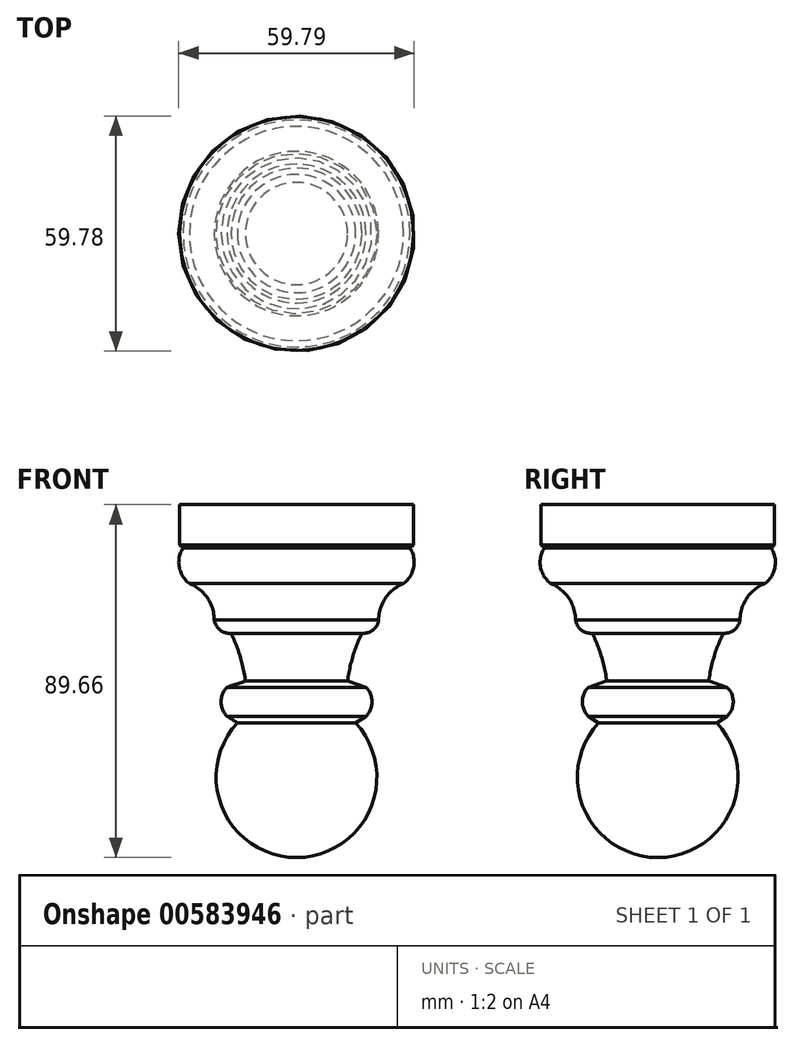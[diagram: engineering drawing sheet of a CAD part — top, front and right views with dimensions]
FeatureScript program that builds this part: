
annotation { "Feature Type Name" : "Feature", "Feature Type Description" : "" }
export const myFeature = defineFeature(function(context is Context, id is Id, definition is map)
    precondition{}
    {
        {
            var Q0;
            Q0=qCreatedBy(makeId("Front.planeOp"),FACE);
            var sketch = newSketch(context, id + "F0", { "sketchPlane" : qUnion([Q0])});
            skLineSegment(sketch, "E0.left", {"start": v(34.75, 61.97) * mm, "end": v(34.75, 51.69) * mm});
            skArc(sketch, "E1", {"start": v(32.3, 41.95) * mm, "mid": v(34.87, 46.17) * mm, "end": v(33.91, 51.02) * mm});
            skLineSegment(sketch, "E2", {"start": v(34.75, 51.69) * mm, "end": v(33.91, 51.02) * mm});
            skArc(sketch, "E3", {"start": v(32.3, 41.95) * mm, "mid": v(27.72, 38.27) * mm, "end": v(25.97, 32.66) * mm});
            skArc(sketch, "E4", {"start": v(21.7, 29.32) * mm, "mid": v(24.5, 30.13) * mm, "end": v(25.97, 32.66) * mm});
            skArc(sketch, "E5", {"start": v(21.7, 29.32) * mm, "mid": v(19.38, 23.38) * mm, "end": v(18.07, 17.13) * mm});
            skLineSegment(sketch, "E6", {"start": v(18.07, 17.13) * mm, "end": v(22.73, 15.6) * mm});
            skArc(sketch, "E7", {"start": v(22.73, 8.23) * mm, "mid": v(24.25, 11.92) * mm, "end": v(22.73, 15.6) * mm});
            skLineSegment(sketch, "E8", {"start": v(22.73, 8.23) * mm, "end": v(20.12, 6.57) * mm});
            skLineSegment(sketch, "E9", {"start": v(5.09, -7.39) * mm, "end": v(5.09, 73.73) * mm});
            skLineSegment(sketch, "E10", {"start": v(5.09, -7.39) * mm, "end": v(5.09, -38.4) * mm});
            skLineSegment(sketch, "E11.right", {"start": v(5.09, 51.69) * mm, "end": v(5.09, 61.97) * mm});
            skLineSegment(sketch, "E12.bottom", {"start": v(34.75, 61.97) * mm, "end": v(5.09, 61.97) * mm});
            skLineSegment(sketch, "E12.right", {"start": v(5.09, 61.97) * mm, "end": v(5.09, 51.69) * mm});
            skArc(sketch, "E13", {"start": v(5.09, -27.69) * mm, "mid": v(23.77, -15.46) * mm, "end": v(20.12, 6.57) * mm});
            skSolve(sketch);
        }
        {
            var Q0;
            Q0=makeQuery(id+"F0.imprint","IMPRINT",FACE,{"disambiguationData":[TD([[makeQuery(id+"F0.imprint","IMPRINT",EDGE,{"derivedFrom":sQuery(id+"F0.wireOp",EDGE,"E3")}),-1.0]])]});
            var Q1;
            Q1=sQuery(id+"F0.wireOp",EDGE,"E13");
            var Q2;
            Q2=sQuery(id+"F0.wireOp",EDGE,"E8");
            var Q3;
            Q3=sQuery(id+"F0.wireOp",EDGE,"E7");
            var Q4;
            Q4=sQuery(id+"F0.wireOp",EDGE,"E6");
            var Q5;
            Q5=sQuery(id+"F0.wireOp",EDGE,"E12.bottom");
            var Q6;
            Q6=sQuery(id+"F0.wireOp",EDGE,"E0.left");
            var Q7;
            Q7=sQuery(id+"F0.wireOp",EDGE,"E1");
            var Q8;
            Q8=sQuery(id+"F0.wireOp",EDGE,"E3");
            var Q9;
            Q9=sQuery(id+"F0.wireOp",EDGE,"E2");
            var Q10;
            Q10=sQuery(id+"F0.wireOp",EDGE,"E4");
            var Q11;
            Q11=sQuery(id+"F0.wireOp",EDGE,"E5");
            var Q12;
            Q12=sQuery(id+"F0.wireOp",EDGE,"E10");
            revolve(context, id + "F1", {"bodyType" : ToolBodyType.SURFACE, "entities" : qUnion([Q0]), "surfaceEntities" : qUnion([Q1, Q2, Q3, Q4, Q5, Q6, Q7, Q8, Q9, Q10, Q11]), "axis" : qUnion([Q12]), "revolveType" : RevolveType.FULL});
        }
    });
